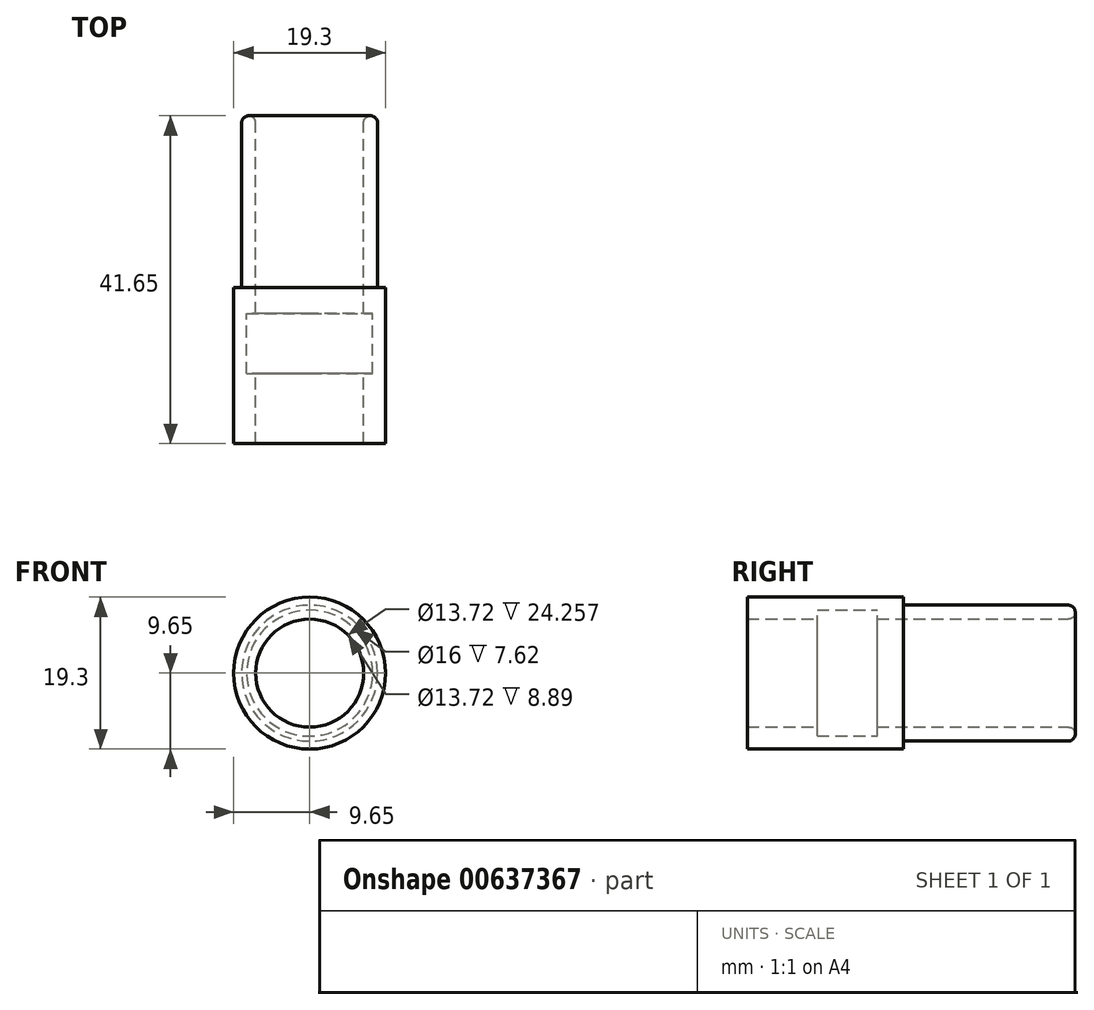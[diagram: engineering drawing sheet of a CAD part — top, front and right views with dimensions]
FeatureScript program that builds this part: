
annotation { "Feature Type Name" : "Feature", "Feature Type Description" : "" }
export const myFeature = defineFeature(function(context is Context, id is Id, definition is map)
    precondition{}
    {
        {
            var Q0;
            Q0=qCreatedBy(makeId("Front.planeOp"),FACE);
            var sketch = newSketch(context, id + "F0", { "sketchPlane" : qUnion([Q0])});
            skCircle(sketch, "E0", {"center": v(0, 0) * mm, "radius": 9.65 * mm});
            skCircle(sketch, "E1", {"center": v(0, 0) * mm, "radius": 6.86 * mm});
            skSolve(sketch);
        }
        {
            var Q0;
            Q0=makeQuery(id+"F0.imprint","IMPRINT",FACE,{"disambiguationData":[TD([[makeQuery(id+"F0.imprint","IMPRINT",EDGE,{"derivedFrom":sQuery(id+"F0.wireOp",EDGE,"E0")}),1.0]])]});
            extrude(context, id + "F1", {"entities" : qUnion([Q0]), "depth" : 3.3 * mm, "offsetDistance" : 25.4 * mm});
        }
        {
            var Q0;
            Q0=makeQuery(id+"F1.opExtrude","CAP_FACE",FACE,{"disambiguationData":[OSD([sQuery(id+"F0.wireOp",EDGE,"E0"),sQuery(id+"F0.wireOp",EDGE,"E1")])],"isStart":false});
            var sketch = newSketch(context, id + "F2", { "sketchPlane" : qUnion([Q0])});
            skCircle(sketch, "E2", {"center": v(0, 0) * mm, "radius": 9.65 * mm});
            skCircle(sketch, "E3", {"center": v(0, 0) * mm, "radius": 8 * mm});
            skSolve(sketch);
        }
        {
            var Q0;
            Q0=makeQuery(id+"F2.imprint","IMPRINT",FACE,{"disambiguationData":[TD([[makeQuery(id+"F2.imprint","IMPRINT",EDGE,{"derivedFrom":sQuery(id+"F2.wireOp",EDGE,"E2")}),1.0]])]});
            extrude(context, id + "F3", {"entities" : qUnion([Q0]), "operationType" : NewBodyOperationType.ADD, "depth" : 7.62 * mm, "offsetDistance" : 25.4 * mm});
        }
        {
            var Q0;
            Q0=makeQuery(id+"F3.opExtrude","CAP_FACE",FACE,{"disambiguationData":[OSD([sQuery(id+"F2.wireOp",EDGE,"E2"),sQuery(id+"F2.wireOp",EDGE,"E3")])],"isStart":false});
            var sketch = newSketch(context, id + "F4", { "sketchPlane" : qUnion([Q0])});
            skCircle(sketch, "E4", {"center": v(0, 0) * mm, "radius": 9.65 * mm});
            skCircle(sketch, "E5", {"center": v(0, 0) * mm, "radius": 6.86 * mm});
            skSolve(sketch);
        }
        {
            var Q0;
            Q0=makeQuery(id+"F4.imprint","IMPRINT",FACE,{"disambiguationData":[TD([[makeQuery(id+"F4.imprint","IMPRINT",EDGE,{"derivedFrom":sQuery(id+"F4.wireOp",EDGE,"E5")}),-1.0]])]});
            var Q1;
            Q1=makeQuery(id+"F4.imprint","IMPRINT",FACE,{"disambiguationData":[TD([[makeQuery(id+"F4.imprint","IMPRINT",EDGE,{"derivedFrom":sQuery(id+"F4.wireOp",EDGE,"E4")}),1.0]])]});
            extrude(context, id + "F5", {"entities" : qUnion([Q0, Q1]), "operationType" : NewBodyOperationType.ADD, "depth" : 8.9 * mm, "offsetDistance" : 25.4 * mm});
        }
        {
            var Q0;
            Q0=makeQuery(id+"F1.opExtrude","CAP_FACE",FACE,{"disambiguationData":[OSD([sQuery(id+"F0.wireOp",EDGE,"E0"),sQuery(id+"F0.wireOp",EDGE,"E1")])],"isStart":true});
            var sketch = newSketch(context, id + "F6", { "sketchPlane" : qUnion([Q0])});
            skCircle(sketch, "E6", {"center": v(0, 0) * mm, "radius": 9.65 * mm});
            skCircle(sketch, "E7", {"center": v(0, 0) * mm, "radius": 6.86 * mm});
            skCircle(sketch, "E8", {"center": v(0, 0) * mm, "radius": 8.64 * mm});
            skSolve(sketch);
        }
        {
            var Q0;
            Q0=makeQuery(id+"F6.imprint","IMPRINT",FACE,{"disambiguationData":[TD([[makeQuery(id+"F6.imprint","IMPRINT",EDGE,{"derivedFrom":sQuery(id+"F6.wireOp",EDGE,"E7")}),1.0]])]});
            extrude(context, id + "F7", {"entities" : qUnion([Q0]), "operationType" : NewBodyOperationType.ADD, "depth" : 21.84 * mm, "offsetDistance" : 25.4 * mm});
        }
        {
            var Q0;
            Q0=makeQuery(id+"F7.opExtrude","CAP_EDGE",EDGE,{"disambiguationData":[OSD([sQuery(id+"F6.wireOp",EDGE,"E7")])],"isStart":false});
            var Q1;
            Q1=makeQuery(id+"F7.opExtrude","CAP_EDGE",EDGE,{"disambiguationData":[OSD([sQuery(id+"F6.wireOp",EDGE,"E8")])],"isStart":false});
            fillet(context, id + "F8", {"entities" : qUnion([Q0, Q1]), "radius" : 0.89 * mm, "tangentPropagation" : true, "allowEdgeOverflow" : false});
        }
    });
